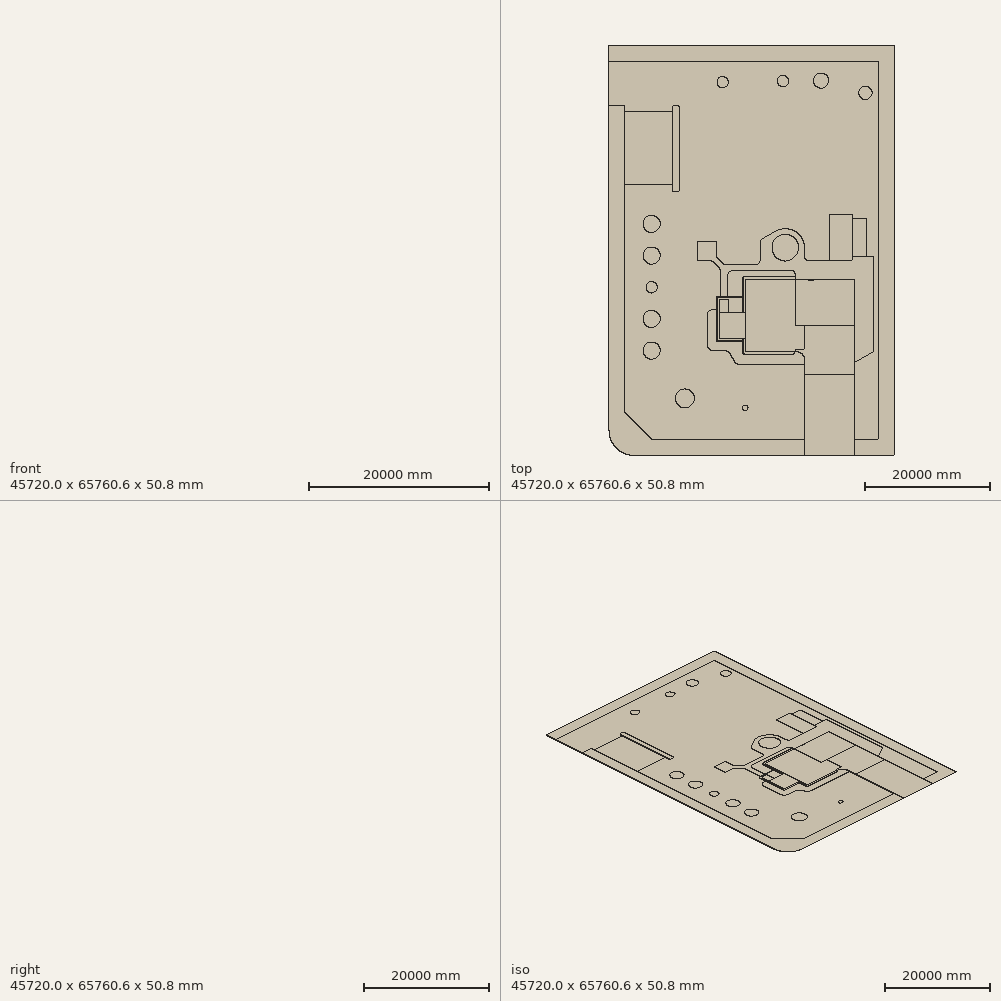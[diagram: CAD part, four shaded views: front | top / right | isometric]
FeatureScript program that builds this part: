
annotation { "Feature Type Name" : "Feature", "Feature Type Description" : "" }
export const myFeature = defineFeature(function(context is Context, id is Id, definition is map)
    precondition{}
    {
        {
            var Q0;
            Q0=qCreatedBy(makeId("Top.planeOp"),FACE);
            var sketch = newSketch(context, id + "F0", { "sketchPlane" : qUnion([Q0])});
            skLineSegment(sketch, "E0.bottom", {"start": v(-22860, 32880.3) * mm, "end": v(22860, 32880.3) * mm});
            skLineSegment(sketch, "E0.top", {"start": v(-18796, -32880.3) * mm, "end": v(22860, -32880.3) * mm});
            skLineSegment(sketch, "E0.left", {"start": v(-22860, 32880.3) * mm, "end": v(-22860, -28816.3) * mm});
            skLineSegment(sketch, "E0.right", {"start": v(22860, 32880.3) * mm, "end": v(22860, -32880.3) * mm});
            skPoint(sketch, "E0.middle", {"position": v(0, 0) * mm});
            skPoint(sketch, "E1.visualSharp", {"position": v(-22860, -32880.3) * mm});
            skArc(sketch, "E1.filletArc", {"start": v(-22860, -28816.3) * mm, "mid": v(-21669.68, -31689.98) * mm, "end": v(-18796, -32880.3) * mm});
            skSolve(sketch);
        }
        {
            var Q0;
            Q0 = qSketchRegion(id + "F0", true);
            extrude(context, id + "F1", {"entities" : qUnion([Q0]), "oppositeDirection" : true, "depth" : 25.4 * mm, "offsetDistance" : 25.4 * mm});
        }
        {
            var Q0;
            Q0=makeQuery(id+"F1.opExtrude","CAP_FACE",FACE,{"disambiguationData":[OSD([sQuery(id+"F0.wireOp",EDGE,"E0.bottom"),sQuery(id+"F0.wireOp",EDGE,"E0.top"),sQuery(id+"F0.wireOp",EDGE,"E0.left"),sQuery(id+"F0.wireOp",EDGE,"E0.right")])],"isStart":true});
            var sketch = newSketch(context, id + "F2", { "sketchPlane" : qUnion([Q0])});
            skLineSegment(sketch, "E2", {"start": v(-914.4, -4635.5) * mm, "end": v(16459.2, -4635.5) * mm});
            skLineSegment(sketch, "E3", {"start": v(16459.2, -4635.5) * mm, "end": v(16459.2, -11950.7) * mm});
            skLineSegment(sketch, "E4", {"start": v(16459.2, -11950.7) * mm, "end": v(7010.4, -11950.7) * mm});
            skLineSegment(sketch, "E5", {"start": v(7010.4, -11950.7) * mm, "end": v(7010.4, -16217.9) * mm});
            skLineSegment(sketch, "E6", {"start": v(7010.4, -16217.9) * mm, "end": v(-914.4, -16217.9) * mm});
            skLineSegment(sketch, "E7", {"start": v(-914.4, -16217.9) * mm, "end": v(-914.4, -4635.5) * mm});
            skSolve(sketch);
        }
        {
            var Q0;
            Q0 = qSketchRegion(id + "F2", true);
            extrude(context, id + "F3", {"entities" : qUnion([Q0]), "depth" : 25.4 * mm, "offsetDistance" : 25.4 * mm});
        }
        {
            var Q0;
            Q0=qCreatedBy(makeId("Top.planeOp"),FACE);
            var sketch = newSketch(context, id + "F4", { "sketchPlane" : qUnion([Q0])});
            skLineSegment(sketch, "E8.bottom", {"start": v(16205.2, -1587.5) * mm, "end": v(12547.6, -1587.5) * mm});
            skLineSegment(sketch, "E8.top", {"start": v(16205.2, 5727.7) * mm, "end": v(12547.6, 5727.7) * mm});
            skLineSegment(sketch, "E8.left", {"start": v(16205.2, -1587.5) * mm, "end": v(16205.2, 5727.7) * mm});
            skLineSegment(sketch, "E8.right", {"start": v(12547.6, -1587.5) * mm, "end": v(12547.6, 5727.7) * mm});
            skPoint(sketch, "E8.middle", {"position": v(14376.4, 2070.1) * mm});
            skSolve(sketch);
        }
        {
            var Q0;
            Q0 = qSketchRegion(id + "F4", true);
            extrude(context, id + "F5", {"entities" : qUnion([Q0]), "depth" : 25.4 * mm, "offsetDistance" : 25.4 * mm});
        }
        {
            var Q0;
            Q0=qCreatedBy(makeId("Top.planeOp"),FACE);
            var sketch = newSketch(context, id + "F6", { "sketchPlane" : qUnion([Q0])});
            skLineSegment(sketch, "E9.bottom", {"start": v(16205.2, 5118.1) * mm, "end": v(18516.6, 5118.1) * mm});
            skLineSegment(sketch, "E9.top", {"start": v(16205.2, -977.9) * mm, "end": v(18516.6, -977.9) * mm});
            skLineSegment(sketch, "E9.left", {"start": v(16205.2, 5118.1) * mm, "end": v(16205.2, -977.9) * mm});
            skLineSegment(sketch, "E9.right", {"start": v(18516.6, 5118.1) * mm, "end": v(18516.6, -977.9) * mm});
            skSolve(sketch);
        }
        {
            var Q0;
            Q0 = qSketchRegion(id + "F6", true);
            extrude(context, id + "F7", {"entities" : qUnion([Q0]), "depth" : 25.4 * mm, "offsetDistance" : 25.4 * mm});
        }
        {
            var Q0;
            Q0=qCreatedBy(makeId("Top.planeOp"),FACE);
            var sketch = newSketch(context, id + "F8", { "sketchPlane" : qUnion([Q0])});
            skLineSegment(sketch, "E10.bottom", {"start": v(-914.4, -9893.3) * mm, "end": v(-5181.6, -9893.3) * mm});
            skLineSegment(sketch, "E10.top", {"start": v(-914.4, -14160.5) * mm, "end": v(-5181.6, -14160.5) * mm});
            skLineSegment(sketch, "E10.left", {"start": v(-914.4, -9893.3) * mm, "end": v(-914.4, -14160.5) * mm});
            skLineSegment(sketch, "E10.right", {"start": v(-5181.6, -9893.3) * mm, "end": v(-5181.6, -14160.5) * mm});
            skSolve(sketch);
        }
        {
            var Q0;
            Q0 = qSketchRegion(id + "F8", true);
            extrude(context, id + "F9", {"entities" : qUnion([Q0]), "depth" : 25.4 * mm, "offsetDistance" : 25.4 * mm});
        }
        {
            var Q0;
            Q0=qCreatedBy(makeId("Top.planeOp"),FACE);
            var sketch = newSketch(context, id + "F10", { "sketchPlane" : qUnion([Q0])});
            skLineSegment(sketch, "E11.bottom", {"start": v(-5181.6, -9893.3) * mm, "end": v(-3657.6, -9893.3) * mm});
            skLineSegment(sketch, "E11.top", {"start": v(-5181.6, -7861.3) * mm, "end": v(-3657.6, -7861.3) * mm});
            skLineSegment(sketch, "E11.left", {"start": v(-5181.6, -9893.3) * mm, "end": v(-5181.6, -7861.3) * mm});
            skLineSegment(sketch, "E11.right", {"start": v(-3657.6, -9893.3) * mm, "end": v(-3657.6, -7861.3) * mm});
            skSolve(sketch);
        }
        {
            var Q0;
            Q0 = qSketchRegion(id + "F10", true);
            extrude(context, id + "F11", {"entities" : qUnion([Q0]), "operationType" : NewBodyOperationType.ADD, "depth" : 25.4 * mm, "offsetDistance" : 25.4 * mm});
        }
        {
            var Q0;
            Q0=makeQuery(id+"F1.opExtrude","CAP_FACE",FACE,{"disambiguationData":[OSD([sQuery(id+"F0.wireOp",EDGE,"E0.bottom"),sQuery(id+"F0.wireOp",EDGE,"E0.top"),sQuery(id+"F0.wireOp",EDGE,"E0.left"),sQuery(id+"F0.wireOp",EDGE,"E0.right"),sQuery(id+"F0.wireOp",EDGE,"E1.filletArc")])],"isStart":true});
            var sketch = newSketch(context, id + "F12", { "sketchPlane" : qUnion([Q0])});
            skLineSegment(sketch, "E12.0", {"start": v(-22860, 32880.3) * mm, "end": v(22860, 32880.3) * mm});
            skLineSegment(sketch, "E13.0", {"start": v(22860, 32880.3) * mm, "end": v(22860, -32880.3) * mm});
            skArc(sketch, "E14.0", {"start": v(-22860, -28816.3) * mm, "mid": v(-21669.68, -31689.98) * mm, "end": v(-18796, -32880.3) * mm});
            skLineSegment(sketch, "E15", {"start": v(-18796, -32880.3) * mm, "end": v(8534.4, -32880.3) * mm});
            skLineSegment(sketch, "E16", {"start": v(8534.4, -32880.3) * mm, "end": v(8534.4, -30340.3) * mm});
            skLineSegment(sketch, "E17", {"start": v(8534.4, -30340.3) * mm, "end": v(-16009.48, -30340.3) * mm});
            skLineSegment(sketch, "E18", {"start": v(-16009.48, -30340.3) * mm, "end": v(-20320, -26029.78) * mm});
            skLineSegment(sketch, "E19", {"start": v(-20320, -26029.78) * mm, "end": v(-20320, 23202.9) * mm});
            skLineSegment(sketch, "E20", {"start": v(-20320, 23202.9) * mm, "end": v(-22860, 23202.9) * mm});
            skLineSegment(sketch, "E21", {"start": v(-22860, 23202.9) * mm, "end": v(-22860, -28816.3) * mm});
            skLineSegment(sketch, "E22", {"start": v(-22860, 32880.3) * mm, "end": v(-22860, 30340.3) * mm});
            skLineSegment(sketch, "E23", {"start": v(-22860, 30340.3) * mm, "end": v(20320, 30340.3) * mm});
            skLineSegment(sketch, "E24", {"start": v(20320, 30340.3) * mm, "end": v(20320, -30340.3) * mm});
            skLineSegment(sketch, "E25", {"start": v(20320, -30340.3) * mm, "end": v(16459.2, -30340.3) * mm});
            skLineSegment(sketch, "E26", {"start": v(16459.2, -30340.3) * mm, "end": v(16459.2, -32880.3) * mm});
            skLineSegment(sketch, "E27", {"start": v(16459.2, -32880.3) * mm, "end": v(22860, -32880.3) * mm});
            skCircle(sketch, "E28", {"center": v(18288, 25260.3) * mm, "radius": 1066.8 * mm});
            skCircle(sketch, "E29", {"center": v(11176, 27241.5) * mm, "radius": 1219.2 * mm});
            skCircle(sketch, "E30", {"center": v(5080, 27148.89) * mm, "radius": 914.4 * mm});
            skCircle(sketch, "E31", {"center": v(-4611.46, 26988.36) * mm, "radius": 914.4 * mm});
            skCircle(sketch, "E32", {"center": v(-16002, 4254.5) * mm, "radius": 1371.6 * mm});
            skCircle(sketch, "E33", {"center": v(-16002, -825.5) * mm, "radius": 1371.6 * mm});
            skCircle(sketch, "E34", {"center": v(-16002, -5905.5) * mm, "radius": 914.4 * mm});
            skCircle(sketch, "E35", {"center": v(-16002, -10985.5) * mm, "radius": 1371.6 * mm});
            skCircle(sketch, "E36", {"center": v(-16002, -16065.5) * mm, "radius": 1371.6 * mm});
            skCircle(sketch, "E37", {"center": v(-10668, -23736.3) * mm, "radius": 1524 * mm});
            skCircle(sketch, "E38", {"center": v(-1016, -25260.3) * mm, "radius": 457.2 * mm});
            skSolve(sketch);
        }
        {
            var Q0;
            Q0 = qSketchRegion(id + "F12", true);
            extrude(context, id + "F13", {"entities" : qUnion([Q0]), "depth" : 6.35 * mm, "offsetDistance" : 25.4 * mm});
        }
        {
            var Q0;
            Q0=qCreatedBy(makeId("Top.planeOp"),FACE);
            var sketch = newSketch(context, id + "F14", { "sketchPlane" : qUnion([Q0])});
            skLineSegment(sketch, "E39", {"start": v(16459.2, -11950.7) * mm, "end": v(16459.2, -19875.5) * mm});
            skLineSegment(sketch, "E40", {"start": v(16459.2, -19875.5) * mm, "end": v(8534.4, -19875.5) * mm});
            skLineSegment(sketch, "E41", {"start": v(8534.4, -19875.5) * mm, "end": v(8534.4, -17589.5) * mm});
            skLineSegment(sketch, "E42.0", {"start": v(7010.4, -11950.7) * mm, "end": v(7010.4, -16217.9) * mm});
            skLineSegment(sketch, "E43.0", {"start": v(16459.2, -11950.7) * mm, "end": v(7010.4, -11950.7) * mm});
            skLineSegment(sketch, "E44", {"start": v(7010.4, -16217.9) * mm, "end": v(7162.8, -16217.9) * mm});
            skArc(sketch, "E45", {"start": v(8534.4, -17589.5) * mm, "mid": v(8132.67, -16619.63) * mm, "end": v(7162.8, -16217.9) * mm});
            skSolve(sketch);
        }
        {
            var Q0;
            Q0 = qSketchRegion(id + "F14", true);
            extrude(context, id + "F15", {"entities" : qUnion([Q0]), "depth" : 12.7 * mm, "offsetDistance" : 25.4 * mm});
        }
        {
            var Q0;
            Q0=makeQuery(id+"F15.opExtrude","CAP_FACE",FACE,{"disambiguationData":[OSD([sQuery(id+"F14.wireOp",EDGE,"E39"),sQuery(id+"F14.wireOp",EDGE,"E40"),sQuery(id+"F14.wireOp",EDGE,"E41"),sQuery(id+"F14.wireOp",EDGE,"E42.0"),sQuery(id+"F14.wireOp",EDGE,"E43.0"),sQuery(id+"F14.wireOp",EDGE,"E44"),sQuery(id+"F14.wireOp",EDGE,"E45")])],"isStart":false});
            var sketch = newSketch(context, id + "F16", { "sketchPlane" : qUnion([Q0])});
            skLineSegment(sketch, "E46.bottom", {"start": v(7010.4, -11950.7) * mm, "end": v(8534.4, -11950.7) * mm});
            skLineSegment(sketch, "E46.top", {"start": v(7010.4, -15913.1) * mm, "end": v(8534.4, -15913.1) * mm});
            skLineSegment(sketch, "E46.left", {"start": v(7010.4, -11950.7) * mm, "end": v(7010.4, -15913.1) * mm});
            skLineSegment(sketch, "E46.right", {"start": v(8534.4, -11950.7) * mm, "end": v(8534.4, -15913.1) * mm});
            skSolve(sketch);
        }
        {
            var Q0;
            Q0 = qSketchRegion(id + "F16", true);
            extrude(context, id + "F17", {"entities" : qUnion([Q0]), "operationType" : NewBodyOperationType.ADD, "depth" : 12.7 * mm, "offsetDistance" : 25.4 * mm});
        }
        {
            var Q0;
            Q0=qCreatedBy(makeId("Top.planeOp"),FACE);
            var sketch = newSketch(context, id + "F18", { "sketchPlane" : qUnion([Q0])});
            skLineSegment(sketch, "E47.bottom", {"start": v(-20320, 22288.5) * mm, "end": v(-12700, 22288.5) * mm});
            skLineSegment(sketch, "E47.top", {"start": v(-20320, 10604.5) * mm, "end": v(-12700, 10604.5) * mm});
            skLineSegment(sketch, "E47.left", {"start": v(-20320, 22288.5) * mm, "end": v(-20320, 10604.5) * mm});
            skLineSegment(sketch, "E47.right", {"start": v(-12700, 22288.5) * mm, "end": v(-12700, 10604.5) * mm});
            skSolve(sketch);
        }
        {
            var Q0;
            Q0 = qSketchRegion(id + "F18", true);
            extrude(context, id + "F19", {"entities" : qUnion([Q0]), "depth" : 12.7 * mm, "offsetDistance" : 25.4 * mm});
        }
        {
            var Q0;
            Q0=qCreatedBy(makeId("Top.planeOp"),FACE);
            var sketch = newSketch(context, id + "F20", { "sketchPlane" : qUnion([Q0])});
            skLineSegment(sketch, "E48.bottom", {"start": v(8534.4, -19875.5) * mm, "end": v(16459.2, -19875.5) * mm});
            skLineSegment(sketch, "E48.top", {"start": v(8534.4, -32880.3) * mm, "end": v(16459.2, -32880.3) * mm});
            skLineSegment(sketch, "E48.left", {"start": v(8534.4, -19875.5) * mm, "end": v(8534.4, -32880.3) * mm});
            skLineSegment(sketch, "E48.right", {"start": v(16459.2, -19875.5) * mm, "end": v(16459.2, -32880.3) * mm});
            skSolve(sketch);
        }
        {
            var Q0;
            Q0 = qSketchRegion(id + "F20", true);
            extrude(context, id + "F21", {"entities" : qUnion([Q0]), "depth" : 12.7 * mm, "offsetDistance" : 25.4 * mm});
        }
        {
            var Q0;
            Q0=qCreatedBy(makeId("Top.planeOp"),FACE);
            var sketch = newSketch(context, id + "F22", { "sketchPlane" : qUnion([Q0])});
            skLineSegment(sketch, "E49.0", {"start": v(7010.4, -16217.9) * mm, "end": v(-914.4, -16217.9) * mm});
            skLineSegment(sketch, "E50.0", {"start": v(-914.4, -16217.9) * mm, "end": v(-914.4, -4635.5) * mm});
            skArc(sketch, "E51", {"start": v(6502.4, -16725.9) * mm, "mid": v(6861.61, -16577.11) * mm, "end": v(7010.4, -16217.9) * mm});
            skLineSegment(sketch, "E52", {"start": v(6502.4, -16725.9) * mm, "end": v(-914.4, -16725.9) * mm});
            skLineSegment(sketch, "E53", {"start": v(-1422.4, -16217.9) * mm, "end": v(-1422.4, -4635.5) * mm});
            skLineSegment(sketch, "E54", {"start": v(-914.4, -4127.5) * mm, "end": v(7010.4, -4127.5) * mm});
            skLineSegment(sketch, "E55", {"start": v(-914.4, -4635.5) * mm, "end": v(7010.4, -4635.5) * mm});
            skLineSegment(sketch, "E56", {"start": v(7010.4, -4127.5) * mm, "end": v(7010.4, -4635.5) * mm});
            skPoint(sketch, "E57.visualSharp", {"position": v(-1422.4, -16725.9) * mm});
            skArc(sketch, "E57.filletArc", {"start": v(-1422.4, -16217.9) * mm, "mid": v(-1273.61, -16577.11) * mm, "end": v(-914.4, -16725.9) * mm});
            skPoint(sketch, "E58.visualSharp", {"position": v(-1422.4, -4127.5) * mm});
            skArc(sketch, "E58.filletArc", {"start": v(-914.4, -4127.5) * mm, "mid": v(-1273.61, -4276.29) * mm, "end": v(-1422.4, -4635.5) * mm});
            skSolve(sketch);
        }
        {
            var Q0;
            Q0 = qSketchRegion(id + "F22", true);
            extrude(context, id + "F23", {"entities" : qUnion([Q0]), "depth" : 12.7 * mm, "offsetDistance" : 25.4 * mm});
        }
        {
            var Q0;
            Q0=makeQuery(id+"F23.opExtrude","CAP_FACE",FACE,{"disambiguationData":[OSD([sQuery(id+"F22.wireOp",EDGE,"E49.0"),sQuery(id+"F22.wireOp",EDGE,"E50.0"),sQuery(id+"F22.wireOp",EDGE,"E51"),sQuery(id+"F22.wireOp",EDGE,"E52"),sQuery(id+"F22.wireOp",EDGE,"E53"),sQuery(id+"F22.wireOp",EDGE,"E54"),sQuery(id+"F22.wireOp",EDGE,"E55"),sQuery(id+"F22.wireOp",EDGE,"E56"),sQuery(id+"F22.wireOp",EDGE,"E57.filletArc"),sQuery(id+"F22.wireOp",EDGE,"E58.filletArc")])],"isStart":false});
            var sketch = newSketch(context, id + "F24", { "sketchPlane" : qUnion([Q0])});
            skArc(sketch, "E59.0", {"start": v(6502.4, -16725.9) * mm, "mid": v(6861.61, -16577.11) * mm, "end": v(7010.4, -16217.9) * mm});
            skLineSegment(sketch, "E60.0", {"start": v(6502.4, -16725.9) * mm, "end": v(-914.4, -16725.9) * mm});
            skArc(sketch, "E61.0", {"start": v(-1422.4, -16217.9) * mm, "mid": v(-1273.61, -16577.11) * mm, "end": v(-914.4, -16725.9) * mm});
            skLineSegment(sketch, "E62.0", {"start": v(-1422.4, -16217.9) * mm, "end": v(-1422.4, -4635.5) * mm});
            skArc(sketch, "E63.0", {"start": v(-914.4, -4127.5) * mm, "mid": v(-1273.61, -4276.29) * mm, "end": v(-1422.4, -4635.5) * mm});
            skLineSegment(sketch, "E64.0", {"start": v(-914.4, -4127.5) * mm, "end": v(7010.4, -4127.5) * mm});
            skLineSegment(sketch, "E65.0", {"start": v(-914.4, -4216.4) * mm, "end": v(7010.4, -4216.4) * mm});
            skArc(sketch, "E65.1", {"start": v(-914.4, -4216.4) * mm, "mid": v(-1210.75, -4339.15) * mm, "end": v(-1333.5, -4635.5) * mm});
            skArc(sketch, "E65.2", {"start": v(6502.4, -16637) * mm, "mid": v(6798.75, -16514.25) * mm, "end": v(6921.5, -16217.9) * mm});
            skLineSegment(sketch, "E65.3", {"start": v(6502.4, -16637) * mm, "end": v(-914.4, -16637) * mm});
            skArc(sketch, "E65.4", {"start": v(-1333.5, -16217.9) * mm, "mid": v(-1210.75, -16514.25) * mm, "end": v(-914.4, -16637) * mm});
            skLineSegment(sketch, "E65.5", {"start": v(-1333.5, -16217.9) * mm, "end": v(-1333.5, -4635.5) * mm});
            skLineSegment(sketch, "E66", {"start": v(7010.4, -4216.4) * mm, "end": v(7010.4, -4127.5) * mm});
            skLineSegment(sketch, "E67", {"start": v(6921.5, -16217.9) * mm, "end": v(7010.4, -16217.9) * mm});
            skSolve(sketch);
        }
        {
            var Q0;
            Q0 = qSketchRegion(id + "F24", true);
            extrude(context, id + "F25", {"entities" : qUnion([Q0]), "depth" : 9.52 * mm, "offsetDistance" : 25.4 * mm});
        }
        {
            var Q0;
            Q0=qCreatedBy(makeId("Top.planeOp"),FACE);
            var sketch = newSketch(context, id + "F26", { "sketchPlane" : qUnion([Q0])});
            skLineSegment(sketch, "E68.bottom", {"start": v(-5588, -7454.9) * mm, "end": v(-1422.4, -7454.9) * mm});
            skLineSegment(sketch, "E68.top", {"start": v(-5588, -14566.9) * mm, "end": v(-1422.4, -14566.9) * mm});
            skLineSegment(sketch, "E68.left", {"start": v(-5588, -7454.9) * mm, "end": v(-5588, -14566.9) * mm});
            skLineSegment(sketch, "E68.right", {"start": v(-1422.4, -7454.9) * mm, "end": v(-1422.4, -14566.9) * mm});
            skSolve(sketch);
        }
        {
            var Q0;
            Q0 = qSketchRegion(id + "F26", true);
            extrude(context, id + "F27", {"entities" : qUnion([Q0]), "depth" : 6.35 * mm, "offsetDistance" : 25.4 * mm});
        }
        {
            var Q0;
            Q0=makeQuery(id+"F27.opExtrude","CAP_FACE",FACE,{"disambiguationData":[OSD([sQuery(id+"F26.wireOp",EDGE,"E68.bottom"),sQuery(id+"F26.wireOp",EDGE,"E68.top"),sQuery(id+"F26.wireOp",EDGE,"E68.left"),sQuery(id+"F26.wireOp",EDGE,"E68.right")])],"isStart":false});
            var sketch = newSketch(context, id + "F28", { "sketchPlane" : qUnion([Q0])});
            skLineSegment(sketch, "E69.0", {"start": v(-5588, -7454.9) * mm, "end": v(-1422.4, -7454.9) * mm});
            skLineSegment(sketch, "E70.0", {"start": v(-5588, -7454.9) * mm, "end": v(-5588, -14566.9) * mm});
            skLineSegment(sketch, "E71.0", {"start": v(-5588, -14566.9) * mm, "end": v(-1422.4, -14566.9) * mm});
            skLineSegment(sketch, "E72.0", {"start": v(-5499.1, -7543.8) * mm, "end": v(-1422.4, -7543.8) * mm});
            skLineSegment(sketch, "E72.1", {"start": v(-5499.1, -7543.8) * mm, "end": v(-5499.1, -14478) * mm});
            skLineSegment(sketch, "E72.2", {"start": v(-5499.1, -14478) * mm, "end": v(-1422.4, -14478) * mm});
            skLineSegment(sketch, "E73", {"start": v(-1422.4, -7454.9) * mm, "end": v(-1422.4, -7543.8) * mm});
            skLineSegment(sketch, "E74", {"start": v(-1422.4, -14478) * mm, "end": v(-1422.4, -14566.9) * mm});
            skSolve(sketch);
        }
        {
            var Q0;
            Q0 = qSketchRegion(id + "F28", true);
            extrude(context, id + "F29", {"entities" : qUnion([Q0]), "depth" : 19.05 * mm, "offsetDistance" : 25.4 * mm});
        }
        {
            var Q0;
            Q0=qCreatedBy(makeId("Top.planeOp"),FACE);
            var sketch = newSketch(context, id + "F30", { "sketchPlane" : qUnion([Q0])});
            skLineSegment(sketch, "E75.0", {"start": v(7010.4, -16217.9) * mm, "end": v(7162.8, -16217.9) * mm});
            skArc(sketch, "E76.0", {"start": v(8534.4, -17589.5) * mm, "mid": v(8132.67, -16619.63) * mm, "end": v(7162.8, -16217.9) * mm});
            skArc(sketch, "E77.0", {"start": v(6502.4, -16725.9) * mm, "mid": v(6861.61, -16577.11) * mm, "end": v(7010.4, -16217.9) * mm});
            skLineSegment(sketch, "E78.0", {"start": v(6502.4, -16725.9) * mm, "end": v(-914.4, -16725.9) * mm});
            skArc(sketch, "E79.0", {"start": v(-1422.4, -16217.9) * mm, "mid": v(-1273.61, -16577.11) * mm, "end": v(-914.4, -16725.9) * mm});
            skLineSegment(sketch, "E80.0", {"start": v(-5588, -14566.9) * mm, "end": v(-1422.4, -14566.9) * mm});
            skLineSegment(sketch, "E81", {"start": v(-1422.4, -16217.9) * mm, "end": v(-1422.4, -14566.9) * mm});
            skLineSegment(sketch, "E82", {"start": v(-5588, -14566.9) * mm, "end": v(-5588, -9486.9) * mm});
            skLineSegment(sketch, "E83", {"start": v(-5588, -9486.9) * mm, "end": v(-6096, -9486.9) * mm});
            skLineSegment(sketch, "E84", {"start": v(-7112, -10502.9) * mm, "end": v(-7112, -15074.9) * mm});
            skLineSegment(sketch, "E85", {"start": v(8534.4, -17589.5) * mm, "end": v(8534.4, -18249.9) * mm});
            skLineSegment(sketch, "E86", {"start": v(8534.4, -18249.9) * mm, "end": v(-1879.6, -18249.9) * mm});
            skArc(sketch, "E87", {"start": v(-2759.48, -17741.9) * mm, "mid": v(-2387.6, -18113.78) * mm, "end": v(-1879.6, -18249.9) * mm});
            skLineSegment(sketch, "E88", {"start": v(-2759.48, -17741.9) * mm, "end": v(-3419.4, -16598.9) * mm});
            skArc(sketch, "E89", {"start": v(-3419.4, -16598.9) * mm, "mid": v(-3791.27, -16227.02) * mm, "end": v(-4299.27, -16090.9) * mm});
            skLineSegment(sketch, "E90", {"start": v(-4299.27, -16090.9) * mm, "end": v(-6096, -16090.9) * mm});
            skArc(sketch, "E91", {"start": v(-7112, -15074.9) * mm, "mid": v(-6814.42, -15793.32) * mm, "end": v(-6096, -16090.9) * mm});
            skPoint(sketch, "E92.visualSharp", {"position": v(-7112, -9486.9) * mm});
            skArc(sketch, "E92.filletArc", {"start": v(-6096, -9486.9) * mm, "mid": v(-6814.42, -9784.48) * mm, "end": v(-7112, -10502.9) * mm});
            skSolve(sketch);
        }
        {
            var Q0;
            Q0 = qSketchRegion(id + "F30", true);
            extrude(context, id + "F31", {"entities" : qUnion([Q0]), "depth" : 6.35 * mm, "offsetDistance" : 25.4 * mm});
        }
        {
            var Q0;
            Q0=makeQuery(id+"F11.boolean.opBoolean","MERGE",FACE,{"derivedFrom":[makeQuery(id+"F9.opExtrude","CAP_FACE",FACE,{"disambiguationData":[OSD([sQuery(id+"F8.wireOp",EDGE,"E10.bottom"),sQuery(id+"F8.wireOp",EDGE,"E10.top"),sQuery(id+"F8.wireOp",EDGE,"E10.left"),sQuery(id+"F8.wireOp",EDGE,"E10.right")])],"isStart":false}),makeQuery(id+"F11.opExtrude","CAP_FACE",FACE,{"disambiguationData":[OSD([sQuery(id+"F10.wireOp",EDGE,"E11.bottom"),sQuery(id+"F10.wireOp",EDGE,"E11.top"),sQuery(id+"F10.wireOp",EDGE,"E11.left"),sQuery(id+"F10.wireOp",EDGE,"E11.right")])],"isStart":false})]});
            var sketch = newSketch(context, id + "F32", { "sketchPlane" : qUnion([Q0])});
            skLineSegment(sketch, "E93.bottom", {"start": v(-5181.6, -7861.3) * mm, "end": v(-3657.6, -7861.3) * mm});
            skLineSegment(sketch, "E93.top", {"start": v(-5181.6, -9893.3) * mm, "end": v(-3657.6, -9893.3) * mm});
            skLineSegment(sketch, "E93.left", {"start": v(-5181.6, -7861.3) * mm, "end": v(-5181.6, -9893.3) * mm});
            skLineSegment(sketch, "E93.right", {"start": v(-3657.6, -7861.3) * mm, "end": v(-3657.6, -9893.3) * mm});
            skSolve(sketch);
        }
        {
            var Q0;
            Q0 = qSketchRegion(id + "F32", true);
            extrude(context, id + "F33", {"entities" : qUnion([Q0]), "operationType" : NewBodyOperationType.REMOVE, "oppositeDirection" : true, "depth" : 3.17 * mm, "offsetDistance" : 25.4 * mm});
        }
        {
            var Q0;
            Q0=qCreatedBy(makeId("Top.planeOp"),FACE);
            var sketch = newSketch(context, id + "F34", { "sketchPlane" : qUnion([Q0])});
            skLineSegment(sketch, "E94.bottom", {"start": v(-12293.6, 23202.9) * mm, "end": v(-11887.2, 23202.9) * mm});
            skLineSegment(sketch, "E94.top", {"start": v(-12293.6, 9385.3) * mm, "end": v(-11887.2, 9385.3) * mm});
            skLineSegment(sketch, "E94.left", {"start": v(-12700, 22796.5) * mm, "end": v(-12700, 9791.7) * mm});
            skLineSegment(sketch, "E94.right", {"start": v(-11480.8, 22796.5) * mm, "end": v(-11480.8, 9791.7) * mm});
            skPoint(sketch, "E95.visualSharp", {"position": v(-11480.8, 23202.9) * mm});
            skArc(sketch, "E95.filletArc", {"start": v(-11480.8, 22796.5) * mm, "mid": v(-11599.83, 23083.87) * mm, "end": v(-11887.2, 23202.9) * mm});
            skPoint(sketch, "E96.visualSharp", {"position": v(-12700, 23202.9) * mm});
            skArc(sketch, "E96.filletArc", {"start": v(-12293.6, 23202.9) * mm, "mid": v(-12580.97, 23083.87) * mm, "end": v(-12700, 22796.5) * mm});
            skPoint(sketch, "E97.visualSharp", {"position": v(-11480.8, 9385.3) * mm});
            skArc(sketch, "E97.filletArc", {"start": v(-11887.2, 9385.3) * mm, "mid": v(-11599.83, 9504.33) * mm, "end": v(-11480.8, 9791.7) * mm});
            skPoint(sketch, "E98.visualSharp", {"position": v(-12700, 9385.3) * mm});
            skArc(sketch, "E98.filletArc", {"start": v(-12700, 9791.7) * mm, "mid": v(-12580.97, 9504.33) * mm, "end": v(-12293.6, 9385.3) * mm});
            skSolve(sketch);
        }
        {
            var Q0;
            Q0 = qSketchRegion(id + "F34", true);
            extrude(context, id + "F35", {"entities" : qUnion([Q0]), "depth" : 25.4 * mm, "offsetDistance" : 25.4 * mm});
        }
        {
            var Q0;
            Q0=makeQuery(id+"F3.opExtrude","CAP_FACE",FACE,{"disambiguationData":[OSD([sQuery(id+"F2.wireOp",EDGE,"E2"),sQuery(id+"F2.wireOp",EDGE,"E3"),sQuery(id+"F2.wireOp",EDGE,"E4"),sQuery(id+"F2.wireOp",EDGE,"E5"),sQuery(id+"F2.wireOp",EDGE,"E6"),sQuery(id+"F2.wireOp",EDGE,"E7")])],"isStart":false});
            var sketch = newSketch(context, id + "F36", { "sketchPlane" : qUnion([Q0])});
            skLineSegment(sketch, "E99.bottom", {"start": v(16459.2, -4635.5) * mm, "end": v(7010.4, -4635.5) * mm});
            skLineSegment(sketch, "E99.top", {"start": v(16459.2, -11950.7) * mm, "end": v(7010.4, -11950.7) * mm});
            skLineSegment(sketch, "E99.left", {"start": v(16459.2, -4635.5) * mm, "end": v(16459.2, -11950.7) * mm});
            skLineSegment(sketch, "E99.right", {"start": v(7010.4, -4635.5) * mm, "end": v(7010.4, -11950.7) * mm});
            skSolve(sketch);
        }
        {
            var Q0;
            Q0 = qSketchRegion(id + "F36", true);
            extrude(context, id + "F37", {"entities" : qUnion([Q0]), "operationType" : NewBodyOperationType.REMOVE, "oppositeDirection" : true, "depth" : 3.17 * mm, "offsetDistance" : 25.4 * mm});
        }
        {
            var Q0;
            Q0=makeQuery(id+"F37.boolean.opBoolean","COPY",FACE,{"derivedFrom":makeQuery(id+"F37.opExtrude","CAP_FACE",FACE,{"disambiguationData":[OSD([sQuery(id+"F36.wireOp",EDGE,"E99.bottom"),sQuery(id+"F36.wireOp",EDGE,"E99.top"),sQuery(id+"F36.wireOp",EDGE,"E99.left"),sQuery(id+"F36.wireOp",EDGE,"E99.right")])],"isStart":false})});
            var sketch = newSketch(context, id + "F38", { "sketchPlane" : qUnion([Q0])});
            skLineSegment(sketch, "E100.bottom", {"start": v(9144, -4635.5) * mm, "end": v(10058.4, -4635.5) * mm});
            skLineSegment(sketch, "E100.top", {"start": v(9144, -4749.8) * mm, "end": v(10058.4, -4749.8) * mm});
            skLineSegment(sketch, "E100.left", {"start": v(9144, -4635.5) * mm, "end": v(9144, -4749.8) * mm});
            skLineSegment(sketch, "E100.right", {"start": v(10058.4, -4635.5) * mm, "end": v(10058.4, -4749.8) * mm});
            skSolve(sketch);
        }
        {
            var Q0;
            Q0 = qSketchRegion(id + "F38", true);
            extrude(context, id + "F39", {"entities" : qUnion([Q0]), "operationType" : NewBodyOperationType.REMOVE, "oppositeDirection" : true, "depth" : 3.17 * mm, "offsetDistance" : 25.4 * mm});
        }
        {
            var Q0;
            Q0=qCreatedBy(makeId("Top.planeOp"),FACE);
            var sketch = newSketch(context, id + "F40", { "sketchPlane" : qUnion([Q0])});
            skLineSegment(sketch, "E101", {"start": v(7010.4, -4635.5) * mm, "end": v(16459.2, -4635.5) * mm});
            skLineSegment(sketch, "E102", {"start": v(16459.2, -4635.5) * mm, "end": v(16459.2, -18046.7) * mm});
            skLineSegment(sketch, "E103", {"start": v(16459.2, -18046.7) * mm, "end": v(19507.2, -16286.94) * mm});
            skLineSegment(sketch, "E104", {"start": v(19507.2, -16286.94) * mm, "end": v(19507.2, -977.9) * mm});
            skLineSegment(sketch, "E105", {"start": v(7010.4, -4635.5) * mm, "end": v(7010.4, -3822.7) * mm});
            skLineSegment(sketch, "E106.0", {"start": v(16205.2, -977.9) * mm, "end": v(19507.2, -977.9) * mm});
            skLineSegment(sketch, "E107", {"start": v(16205.2, -977.9) * mm, "end": v(16205.2, -1587.5) * mm});
            skLineSegment(sketch, "E108", {"start": v(16205.2, -1587.5) * mm, "end": v(9093.2, -1587.5) * mm});
            skLineSegment(sketch, "E109", {"start": v(-5029.2, -7454.9) * mm, "end": v(-3810, -7454.9) * mm});
            skLineSegment(sketch, "E110", {"start": v(-5029.2, -7454.9) * mm, "end": v(-5029.2, -3197.78) * mm});
            skLineSegment(sketch, "E111", {"start": v(-2895.6, -3213.1) * mm, "end": v(6400.8, -3213.1) * mm});
            skCircle(sketch, "E112", {"center": v(5435.6, 444.5) * mm, "radius": 2743.2 * mm, "construction": true});
            skLineSegment(sketch, "E113", {"start": v(-3810, -7454.9) * mm, "end": v(-3810, -4127.5) * mm});
            skPoint(sketch, "E114.visualSharp", {"position": v(-3810, -3213.1) * mm});
            skArc(sketch, "E114.filletArc", {"start": v(-2895.6, -3213.1) * mm, "mid": v(-3542.18, -3480.92) * mm, "end": v(-3810, -4127.5) * mm});
            skLineSegment(sketch, "E115", {"start": v(-4130.12, -2298.7) * mm, "end": v(762, -2298.7) * mm});
            skPoint(sketch, "E116.visualSharp", {"position": v(-2009.2, -2298.7) * mm});
            skArc(sketch, "E117", {"start": v(8483.6, 444.5) * mm, "mid": v(6959.6, 3084.15) * mm, "end": v(3911.6, 3084.15) * mm});
            skPoint(sketch, "E118.visualSharp", {"position": v(2715.2, -2298.7) * mm});
            skLineSegment(sketch, "E119", {"start": v(8483.6, 444.5) * mm, "end": v(8483.6, -977.9) * mm});
            skCircle(sketch, "E120", {"center": v(5435.6, 444.5) * mm, "radius": 2133.6 * mm});
            skLineSegment(sketch, "E121", {"start": v(1371.6, -1689.1) * mm, "end": v(1371.6, 1265.72) * mm});
            skLineSegment(sketch, "E122", {"start": v(1676.4, 1793.65) * mm, "end": v(3911.6, 3084.15) * mm});
            skLineSegment(sketch, "E123", {"start": v(-5207.75, -2766.73) * mm, "end": v(-6143.8, -1830.67) * mm});
            skLineSegment(sketch, "E124", {"start": v(-6574.86, -1652.12) * mm, "end": v(-8723.78, -1652.12) * mm});
            skLineSegment(sketch, "E125", {"start": v(-8723.78, -1652.12) * mm, "end": v(-8723.78, 1395.88) * mm});
            skLineSegment(sketch, "E126", {"start": v(-8723.78, 1395.88) * mm, "end": v(-5675.78, 1395.88) * mm});
            skLineSegment(sketch, "E127", {"start": v(-5675.78, 1395.88) * mm, "end": v(-5675.78, -753.04) * mm});
            skLineSegment(sketch, "E128", {"start": v(-5497.23, -1184.1) * mm, "end": v(-4561.17, -2120.15) * mm});
            skLineSegment(sketch, "E129", {"start": v(-4382.62, -2298.7) * mm, "end": v(-5029.2, -2945.28) * mm, "construction": true});
            skPoint(sketch, "E130.visualSharp", {"position": v(7010.4, -3213.1) * mm});
            skArc(sketch, "E130.filletArc", {"start": v(7010.4, -3822.7) * mm, "mid": v(6831.85, -3391.65) * mm, "end": v(6400.8, -3213.1) * mm});
            skPoint(sketch, "E131.visualSharp", {"position": v(8483.6, -1587.5) * mm});
            skArc(sketch, "E131.filletArc", {"start": v(8483.6, -977.9) * mm, "mid": v(8662.15, -1408.95) * mm, "end": v(9093.2, -1587.5) * mm});
            skPoint(sketch, "E132.visualSharp", {"position": v(1371.6, -2298.7) * mm});
            skArc(sketch, "E132.filletArc", {"start": v(762, -2298.7) * mm, "mid": v(1193.05, -2120.15) * mm, "end": v(1371.6, -1689.1) * mm});
            skPoint(sketch, "E133.visualSharp", {"position": v(1371.6, 1617.68) * mm});
            skArc(sketch, "E133.filletArc", {"start": v(1676.4, 1793.65) * mm, "mid": v(1453.27, 1570.52) * mm, "end": v(1371.6, 1265.72) * mm});
            skPoint(sketch, "E134.visualSharp", {"position": v(-4382.62, -2298.7) * mm});
            skArc(sketch, "E134.filletArc", {"start": v(-4561.17, -2120.15) * mm, "mid": v(-4363.4, -2252.3) * mm, "end": v(-4130.12, -2298.7) * mm});
            skPoint(sketch, "E135.visualSharp", {"position": v(-5029.2, -2945.28) * mm});
            skArc(sketch, "E135.filletArc", {"start": v(-5029.2, -3197.78) * mm, "mid": v(-5075.6, -2964.5) * mm, "end": v(-5207.75, -2766.73) * mm});
            skPoint(sketch, "E136.visualSharp", {"position": v(-6322.36, -1652.12) * mm});
            skArc(sketch, "E136.filletArc", {"start": v(-6143.8, -1830.67) * mm, "mid": v(-6341.58, -1698.52) * mm, "end": v(-6574.86, -1652.12) * mm});
            skPoint(sketch, "E137.visualSharp", {"position": v(-5675.78, -1005.54) * mm});
            skArc(sketch, "E137.filletArc", {"start": v(-5675.78, -753.04) * mm, "mid": v(-5629.38, -986.32) * mm, "end": v(-5497.23, -1184.1) * mm});
            skSolve(sketch);
        }
        {
            var Q0;
            Q0 = qSketchRegion(id + "F40", true);
            extrude(context, id + "F41", {"entities" : qUnion([Q0]), "depth" : 25.4 * mm, "offsetDistance" : 25.4 * mm});
        }
    });
